# Revit family: 2-5134-24 Fuse
name_source: partatom
category: Lighting Fixtures
revit_build: Autodesk Revit LT 2014 (Build: 20130308_1515(x64)
units: mm (PartAtom-declared; Revit-internal decimal feet)

## types (1)
- 2-5134-24 Fuse
    ADA Compliant = Yes
    Apparent Load = 34 VA
    Color Filter = 16777215
    Default Elevation = 4' - 0"
    Description = 26" LED Vanity
    Diffuser = Matte White Acrylic
    Dimming Lamp Color Temperature Shift = <None>
    Emit Shape Visible in Rendering = No
    Emit from Rectangle Length = 4' - 0"
    Emit from Rectangle Width = 2' - 0"
    Fixture Depth = 0' - 3 15/16"
    Fixture Height = 0' - 5 3/16"
    Fixture Length = 2' - 2 15/32"
    Input Power (Watts) = 34W
    Input Voltage (Volts AC) = 120
    Junction Box = 4" Octagonal
    Lamp = 2x17W T8 fluorescent
    Lamp Manufacturer = Sylvania
    Manufacturer = Oxygen Lighting
    Metal Finish = Satin Finish
    Model = 2-5134-24
    Photometric Web File = generic
    Product Documentation Link = http://oxygenlighting.com.s3.amazonaws.com
    Tilt Angle = 60.00°
    Type Comments = Lighting - Fluorescent
    URL = http://www.oxygenlighting.com

## geometry (parser evidence)
native form markers: Sweep x1
no freeform markers — native parametric forms only
